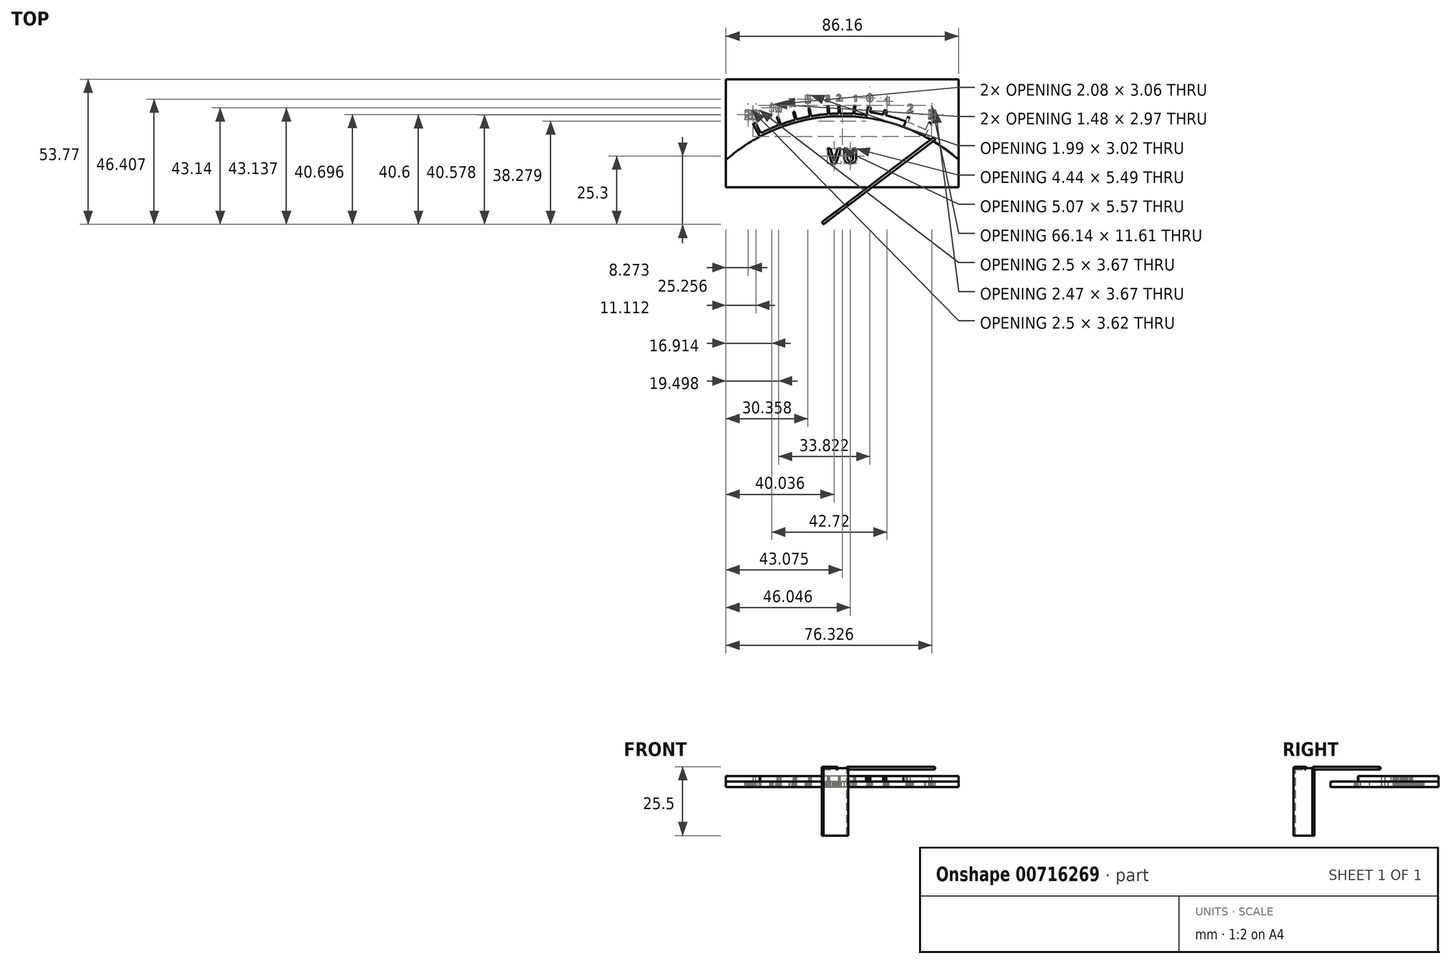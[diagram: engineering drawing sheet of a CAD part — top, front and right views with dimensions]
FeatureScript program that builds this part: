
annotation { "Feature Type Name" : "Feature", "Feature Type Description" : "" }
export const myFeature = defineFeature(function(context is Context, id is Id, definition is map)
    precondition{}
    {
        {
            var Q0;
            Q0=qCreatedBy(makeId("Top.planeOp"),FACE);
            var sketch = newSketch(context, id + "F0", { "sketchPlane" : qUnion([Q0])});
            skLineSegment(sketch, "E0.bottom", {"start": v(-47.11, 47.11) * mm, "end": v(47.11, 47.11) * mm, "construction": true});
            skLineSegment(sketch, "E0.top", {"start": v(-47.11, -47.11) * mm, "end": v(47.11, -47.11) * mm, "construction": true});
            skLineSegment(sketch, "E0.left", {"start": v(-47.11, 47.11) * mm, "end": v(-47.11, -47.11) * mm, "construction": true});
            skLineSegment(sketch, "E0.right", {"start": v(51.21, 42.43) * mm, "end": v(51.21, -51.8) * mm, "construction": true});
            skLineSegment(sketch, "E1", {"start": v(0, 0) * mm, "end": v(0, 47.11) * mm, "construction": true});
            skLineSegment(sketch, "E2.bottom", {"start": v(-43.08, 19.18) * mm, "end": v(43.08, 19.18) * mm});
            skLineSegment(sketch, "E2.top", {"start": v(-43.08, -20.84) * mm, "end": v(43.08, -20.84) * mm});
            skLineSegment(sketch, "E2.left", {"start": v(-43.08, 19.18) * mm, "end": v(-43.08, -20.84) * mm});
            skLineSegment(sketch, "E2.right", {"start": v(43.08, 19.18) * mm, "end": v(43.08, -20.84) * mm});
            skLineSegment(sketch, "E3", {"start": v(0, 0) * mm, "end": v(0, 19.18) * mm});
            skLineSegment(sketch, "E4", {"start": v(-43.08, -6.5) * mm, "end": v(-5.58, -6.5) * mm, "construction": true});
            skLineSegment(sketch, "E5", {"start": v(-31.08, 0) * mm, "end": v(-43.08, 0) * mm});
            skText(sketch, "E6", { "text": "V", "fontName": "OpenSans-Bold.ttf"});
            skText(sketch, "E7", { "text": "U", "fontName": "OpenSans-Bold.ttf"});
            skLineSegment(sketch, "E8", {"start": v(0, -6.5) * mm, "end": v(0.1, -6.5) * mm});
            skLineSegment(sketch, "E9", {"start": v(42.92, 0) * mm, "end": v(30.92, 0) * mm});
            skLineSegment(sketch, "E10", {"start": v(-33.08, 19.18) * mm, "end": v(-33.08, -21) * mm, "construction": true});
            skLineSegment(sketch, "E11", {"start": v(-23.08, 19.18) * mm, "end": v(-23.08, -21) * mm, "construction": true});
            skLineSegment(sketch, "E12", {"start": v(-13.08, 19.18) * mm, "end": v(-13.08, -21) * mm, "construction": true});
            skLineSegment(sketch, "E13", {"start": v(-3.08, 19.18) * mm, "end": v(-3.08, -21) * mm, "construction": true});
            skLineSegment(sketch, "E14", {"start": v(6.92, 19.18) * mm, "end": v(6.92, -21) * mm, "construction": true});
            skLineSegment(sketch, "E15", {"start": v(16.92, 19.18) * mm, "end": v(16.92, -21) * mm, "construction": true});
            skLineSegment(sketch, "E16", {"start": v(26.92, 19.18) * mm, "end": v(26.92, -20.84) * mm, "construction": true});
            skLineSegment(sketch, "E17", {"start": v(36.92, 19.18) * mm, "end": v(36.92, -20.84) * mm, "construction": true});
            skLineSegment(sketch, "E18", {"start": v(-43.08, 9.18) * mm, "end": v(42.92, 9.18) * mm, "construction": true});
            skLineSegment(sketch, "E19", {"start": v(-43.08, -0.82) * mm, "end": v(42.92, -0.82) * mm, "construction": true});
            skLineSegment(sketch, "E20", {"start": v(-43.08, -10.82) * mm, "end": v(42.92, -10.82) * mm, "construction": true});
            skLineSegment(sketch, "E21", {"start": v(0, 0) * mm, "end": v(0.1, -60) * mm});
            skCircle(sketch, "E22", {"center": v(0.1, -60) * mm, "radius": 65.5 * mm});
            skCircle(sketch, "E23", {"center": v(0.1, -60) * mm, "radius": 66.5 * mm});
            skLineSegment(sketch, "E24", {"start": v(0.1, -60) * mm, "end": v(-33.08, 2.65) * mm});
            skLineSegment(sketch, "E25", {"start": v(0.1, -60) * mm, "end": v(-32.19, 3.1) * mm});
            skCircle(sketch, "E26", {"center": v(0.1, -60) * mm, "radius": 70.89 * mm});
            skLineSegment(sketch, "E27", {"start": v(0.1, -60) * mm, "end": v(33.07, 2.76) * mm});
            skLineSegment(sketch, "E28", {"start": v(0.1, -60) * mm, "end": v(32.18, 3.22) * mm});
            skCircle(sketch, "E29", {"center": v(0.1, -60) * mm, "radius": 67.75 * mm});
            skCircle(sketch, "E30", {"center": v(0.1, -60) * mm, "radius": 69.5 * mm});
            skLineSegment(sketch, "E31", {"start": v(0.1, -60) * mm, "end": v(9.42, 8.87) * mm});
            skLineSegment(sketch, "E32", {"start": v(0.1, -60) * mm, "end": v(10.62, 8.7) * mm});
            skLineSegment(sketch, "E33", {"start": v(0.1, -60) * mm, "end": v(-24.25, 5.1) * mm});
            skLineSegment(sketch, "E34", {"start": v(0.1, -60) * mm, "end": v(-23.78, 5.27) * mm});
            skLineSegment(sketch, "E35", {"start": v(0.1, -60) * mm, "end": v(-18.25, 7.03) * mm});
            skLineSegment(sketch, "E36", {"start": v(0.1, -60) * mm, "end": v(-17.77, 7.16) * mm});
            skLineSegment(sketch, "E37", {"start": v(0.1, -60) * mm, "end": v(-12.08, 8.42) * mm});
            skLineSegment(sketch, "E38", {"start": v(-12.57, 8.33) * mm, "end": v(0.1, -60) * mm});
            skLineSegment(sketch, "E39", {"start": v(0.1, -60) * mm, "end": v(-5.49, 9.27) * mm});
            skLineSegment(sketch, "E40", {"start": v(0.1, -60) * mm, "end": v(-5, 9.31) * mm});
            skLineSegment(sketch, "E41", {"start": v(0.1, -60) * mm, "end": v(-1.42, 9.48) * mm});
            skLineSegment(sketch, "E42", {"start": v(0.1, -60) * mm, "end": v(-0.92, 9.5) * mm});
            skLineSegment(sketch, "E43", {"start": v(0.1, -60) * mm, "end": v(4.35, 9.37) * mm});
            skLineSegment(sketch, "E44", {"start": v(0.1, -60) * mm, "end": v(4.85, 9.34) * mm});
            skLineSegment(sketch, "E45", {"start": v(0.1, -60) * mm, "end": v(15.62, 7.74) * mm});
            skLineSegment(sketch, "E46", {"start": v(0.1, -60) * mm, "end": v(16.6, 7.51) * mm});
            skLineSegment(sketch, "E47", {"start": v(0.1, -60) * mm, "end": v(24.1, 5.23) * mm});
            skLineSegment(sketch, "E48", {"start": v(0.1, -60) * mm, "end": v(25.03, 4.87) * mm});
            skCircle(sketch, "E49", {"center": v(0.1, -60) * mm, "radius": 71.64 * mm, "construction": true});
            const initialGuessF0  = {"E6": [-0.00558, -0.01212, 1, 0, 0.00562], "E7": [0.0001, -0.01196, 1, 0, 0.00546]};
            skSetInitialGuess(sketch, initialGuessF0);
            skSolve(sketch);
        }
        {
            var Q0;
            {var subQ0=sQuery(id+"F0.wireOp",EDGE,"E2.left");var subQ1=sQuery(id+"F0.wireOp",EDGE,"E2.top");var subQ2=makeQuery(id+"F0.imprint","INTERSECT",VERTEX,{"derivedFrom":[subQ1,subQ0]});Q0=makeQuery(id+"F0.imprint","IMPRINT",FACE,{"disambiguationData":[TD([[makeQuery(id+"F0.imprint","IMPRINT",EDGE,{"disambiguationData":[TD([[subQ2,-1.0]])],"derivedFrom":subQ1}),1.0]])]});}
            var Q1;
            Q1=makeQuery(id+"F0.imprint","IMPRINT",FACE,{"disambiguationData":[TD([[makeQuery(id+"F0.imprint","IMPRINT",EDGE,{"derivedFrom":sQuery(id+"F0.wireOp",EDGE,"E6.sketch_text.stroke-0")}),1.0]])]});
            var Q2;
            {var subQ0=sQuery(id+"F0.wireOp",EDGE,"E23");var subQ1=sQuery(id+"F0.wireOp",EDGE,"E2.left");var subQ2=makeQuery(id+"F0.imprint","INTERSECT",VERTEX,{"derivedFrom":[subQ1,subQ0]});Q2=makeQuery(id+"F0.imprint","IMPRINT",FACE,{"disambiguationData":[TD([[makeQuery(id+"F0.imprint","IMPRINT",EDGE,{"disambiguationData":[TD([[subQ2,-1.0]])],"derivedFrom":subQ1}),1.0]])]});}
            var Q3;
            {var subQ5=sQuery(id+"F0.wireOp",EDGE,"E26");var subQ6=sQuery(id+"F0.wireOp",EDGE,"E2.left");var subQ7=makeQuery(id+"F0.imprint","INTERSECT",VERTEX,{"derivedFrom":[subQ6,subQ5]});Q3=makeQuery(id+"F0.imprint","IMPRINT",FACE,{"disambiguationData":[TD([[makeQuery(id+"F0.imprint","IMPRINT",EDGE,{"disambiguationData":[TD([[subQ7,-1.0]])],"derivedFrom":subQ6}),1.0]])]});}
            var Q4;
            {var subQ1=sQuery(id+"F0.wireOp",EDGE,"E2.left");var subQ5=sQuery(id+"F0.wireOp",EDGE,"E2.bottom");var subQ6=makeQuery(id+"F0.imprint","INTERSECT",VERTEX,{"derivedFrom":[subQ5,subQ1]});Q4=makeQuery(id+"F0.imprint","IMPRINT",FACE,{"disambiguationData":[TD([[makeQuery(id+"F0.imprint","IMPRINT",EDGE,{"disambiguationData":[TD([[subQ6,-1.0]])],"derivedFrom":subQ5}),-1.0]])]});}
            var Q5;
            {var subQ0=sQuery(id+"F0.wireOp",EDGE,"E23");var subQ1=sQuery(id+"F0.wireOp",EDGE,"E3");var subQ2=makeQuery(id+"F0.imprint","INTERSECT",VERTEX,{"derivedFrom":[subQ1,subQ0]});Q5=makeQuery(id+"F0.imprint","IMPRINT",FACE,{"disambiguationData":[TD([[makeQuery(id+"F0.imprint","IMPRINT",EDGE,{"disambiguationData":[TD([[subQ2,-1.0]])],"derivedFrom":subQ1}),1.0]])]});}
            var Q6;
            {var subQ0=sQuery(id+"F0.wireOp",EDGE,"E23");var subQ1=sQuery(id+"F0.wireOp",EDGE,"E3");var subQ2=makeQuery(id+"F0.imprint","INTERSECT",VERTEX,{"derivedFrom":[subQ1,subQ0]});Q6=makeQuery(id+"F0.imprint","IMPRINT",FACE,{"disambiguationData":[TD([[makeQuery(id+"F0.imprint","IMPRINT",EDGE,{"disambiguationData":[TD([[subQ2,-1.0]])],"derivedFrom":subQ1}),-1.0]])]});}
            var Q7;
            Q7=makeQuery(id+"F0.imprint","IMPRINT",FACE,{"disambiguationData":[TD([[makeQuery(id+"F0.imprint","IMPRINT",EDGE,{"derivedFrom":sQuery(id+"F0.wireOp",EDGE,"E7.sketch_text.stroke-0")}),1.0]])]});
            var Q8;
            {var subQ0=sQuery(id+"F0.wireOp",EDGE,"E2.right");var subQ1=sQuery(id+"F0.wireOp",EDGE,"E2.top");var subQ2=makeQuery(id+"F0.imprint","INTERSECT",VERTEX,{"derivedFrom":[subQ1,subQ0]});Q8=makeQuery(id+"F0.imprint","IMPRINT",FACE,{"disambiguationData":[TD([[makeQuery(id+"F0.imprint","IMPRINT",EDGE,{"disambiguationData":[TD([[subQ2,1.0]])],"derivedFrom":subQ1}),1.0]])]});}
            var Q9;
            {var subQ0=sQuery(id+"F0.wireOp",EDGE,"E26");var subQ6=sQuery(id+"F0.wireOp",EDGE,"E2.right");var subQ9=makeQuery(id+"F0.imprint","INTERSECT",VERTEX,{"derivedFrom":[subQ6,subQ0]});Q9=makeQuery(id+"F0.imprint","IMPRINT",FACE,{"disambiguationData":[TD([[makeQuery(id+"F0.imprint","IMPRINT",EDGE,{"disambiguationData":[TD([[subQ9,-1.0]])],"derivedFrom":subQ6}),-1.0]])]});}
            var Q10;
            {var subQ0=sQuery(id+"F0.wireOp",EDGE,"E23");var subQ1=sQuery(id+"F0.wireOp",EDGE,"E2.right");var subQ2=makeQuery(id+"F0.imprint","INTERSECT",VERTEX,{"derivedFrom":[subQ1,subQ0]});Q10=makeQuery(id+"F0.imprint","IMPRINT",FACE,{"disambiguationData":[TD([[makeQuery(id+"F0.imprint","IMPRINT",EDGE,{"disambiguationData":[TD([[subQ2,-1.0]])],"derivedFrom":subQ1}),-1.0]])]});}
            var Q11;
            {var subQ0=sQuery(id+"F0.wireOp",EDGE,"E26");var subQ1=sQuery(id+"F0.wireOp",EDGE,"E9");var subQ2=makeQuery(id+"F0.imprint","INTERSECT",VERTEX,{"derivedFrom":[subQ1,subQ0]});Q11=makeQuery(id+"F0.imprint","IMPRINT",FACE,{"disambiguationData":[TD([[makeQuery(id+"F0.imprint","IMPRINT",EDGE,{"disambiguationData":[TD([[subQ2,-1.0]])],"derivedFrom":subQ1}),-1.0]])]});}
            var Q12;
            {var subQ1=sQuery(id+"F0.wireOp",EDGE,"E2.right");var subQ5=sQuery(id+"F0.wireOp",EDGE,"E2.bottom");var subQ9=makeQuery(id+"F0.imprint","INTERSECT",VERTEX,{"derivedFrom":[subQ5,subQ1]});Q12=makeQuery(id+"F0.imprint","IMPRINT",FACE,{"disambiguationData":[TD([[makeQuery(id+"F0.imprint","IMPRINT",EDGE,{"disambiguationData":[TD([[subQ9,1.0]])],"derivedFrom":subQ5}),-1.0]])]});}
            var Q13;
            {var subQ0=sQuery(id+"F0.wireOp",EDGE,"E5");var subQ1=sQuery(id+"F0.wireOp",EDGE,"E2.left");var subQ2=makeQuery(id+"F0.imprint","INTERSECT",VERTEX,{"derivedFrom":[subQ1,subQ0]});Q13=makeQuery(id+"F0.imprint","IMPRINT",FACE,{"disambiguationData":[TD([[makeQuery(id+"F0.imprint","IMPRINT",EDGE,{"disambiguationData":[TD([[subQ2,-1.0]])],"derivedFrom":subQ1}),1.0]])]});}
            var Q14;
            {var subQ0=sQuery(id+"F0.wireOp",EDGE,"E24");var subQ1=sQuery(id+"F0.wireOp",EDGE,"E5");var subQ2=makeQuery(id+"F0.imprint","INTERSECT",VERTEX,{"derivedFrom":[subQ1,subQ0]});Q14=makeQuery(id+"F0.imprint","IMPRINT",FACE,{"disambiguationData":[TD([[makeQuery(id+"F0.imprint","IMPRINT",EDGE,{"disambiguationData":[TD([[subQ2,-1.0]])],"derivedFrom":subQ1}),-1.0]])]});}
            var Q15;
            {var subQ0=sQuery(id+"F0.wireOp",EDGE,"E28");var subQ1=sQuery(id+"F0.wireOp",EDGE,"E2.top");var subQ2=makeQuery(id+"F0.imprint","INTERSECT",VERTEX,{"derivedFrom":[subQ1,subQ0]});Q15=makeQuery(id+"F0.imprint","IMPRINT",FACE,{"disambiguationData":[TD([[makeQuery(id+"F0.imprint","IMPRINT",EDGE,{"disambiguationData":[TD([[subQ2,-1.0]])],"derivedFrom":subQ1}),1.0]])]});}
            var Q16;
            {var subQ0=sQuery(id+"F0.wireOp",EDGE,"E24");var subQ1=sQuery(id+"F0.wireOp",EDGE,"E2.top");var subQ2=makeQuery(id+"F0.imprint","INTERSECT",VERTEX,{"derivedFrom":[subQ1,subQ0]});Q16=makeQuery(id+"F0.imprint","IMPRINT",FACE,{"disambiguationData":[TD([[makeQuery(id+"F0.imprint","IMPRINT",EDGE,{"disambiguationData":[TD([[subQ2,-1.0]])],"derivedFrom":subQ1}),1.0]])]});}
            var Q17;
            {var subQ0=sQuery(id+"F0.wireOp",EDGE,"E29");var subQ1=sQuery(id+"F0.wireOp",EDGE,"E2.right");var subQ2=makeQuery(id+"F0.imprint","INTERSECT",VERTEX,{"derivedFrom":[subQ1,subQ0]});Q17=makeQuery(id+"F0.imprint","IMPRINT",FACE,{"disambiguationData":[TD([[makeQuery(id+"F0.imprint","IMPRINT",EDGE,{"disambiguationData":[TD([[subQ2,-1.0]])],"derivedFrom":subQ1}),-1.0]])]});}
            var Q18;
            {var subQ1=sQuery(id+"F0.wireOp",EDGE,"E2.right");var subQ7=sQuery(id+"F0.wireOp",EDGE,"E30");var subQ9=makeQuery(id+"F0.imprint","INTERSECT",VERTEX,{"derivedFrom":[subQ1,subQ7]});Q18=makeQuery(id+"F0.imprint","IMPRINT",FACE,{"disambiguationData":[TD([[makeQuery(id+"F0.imprint","IMPRINT",EDGE,{"disambiguationData":[TD([[subQ9,-1.0]])],"derivedFrom":subQ1}),-1.0]])]});}
            var Q19;
            {var subQ0=sQuery(id+"F0.wireOp",EDGE,"E30");var subQ1=sQuery(id+"F0.wireOp",EDGE,"E9");var subQ2=makeQuery(id+"F0.imprint","INTERSECT",VERTEX,{"derivedFrom":[subQ1,subQ0]});Q19=makeQuery(id+"F0.imprint","IMPRINT",FACE,{"disambiguationData":[TD([[makeQuery(id+"F0.imprint","IMPRINT",EDGE,{"disambiguationData":[TD([[subQ2,-1.0]])],"derivedFrom":subQ1}),-1.0]])]});}
            var Q20;
            {var subQ0=sQuery(id+"F0.wireOp",EDGE,"E30");var subQ1=sQuery(id+"F0.wireOp",EDGE,"E3");var subQ2=makeQuery(id+"F0.imprint","INTERSECT",VERTEX,{"derivedFrom":[subQ1,subQ0]});Q20=makeQuery(id+"F0.imprint","IMPRINT",FACE,{"disambiguationData":[TD([[makeQuery(id+"F0.imprint","IMPRINT",EDGE,{"disambiguationData":[TD([[subQ2,-1.0]])],"derivedFrom":subQ1}),-1.0]])]});}
            var Q21;
            {var subQ0=sQuery(id+"F0.wireOp",EDGE,"E29");var subQ1=sQuery(id+"F0.wireOp",EDGE,"E3");var subQ2=makeQuery(id+"F0.imprint","INTERSECT",VERTEX,{"derivedFrom":[subQ1,subQ0]});Q21=makeQuery(id+"F0.imprint","IMPRINT",FACE,{"disambiguationData":[TD([[makeQuery(id+"F0.imprint","IMPRINT",EDGE,{"disambiguationData":[TD([[subQ2,-1.0]])],"derivedFrom":subQ1}),-1.0]])]});}
            var Q22;
            {var subQ5=sQuery(id+"F0.wireOp",EDGE,"E2.left");var subQ7=sQuery(id+"F0.wireOp",EDGE,"E30");var subQ9=makeQuery(id+"F0.imprint","INTERSECT",VERTEX,{"derivedFrom":[subQ5,subQ7]});Q22=makeQuery(id+"F0.imprint","IMPRINT",FACE,{"disambiguationData":[TD([[makeQuery(id+"F0.imprint","IMPRINT",EDGE,{"disambiguationData":[TD([[subQ9,-1.0]])],"derivedFrom":subQ5}),1.0]])]});}
            var Q23;
            {var subQ0=sQuery(id+"F0.wireOp",EDGE,"E29");var subQ1=sQuery(id+"F0.wireOp",EDGE,"E2.left");var subQ2=makeQuery(id+"F0.imprint","INTERSECT",VERTEX,{"derivedFrom":[subQ1,subQ0]});Q23=makeQuery(id+"F0.imprint","IMPRINT",FACE,{"disambiguationData":[TD([[makeQuery(id+"F0.imprint","IMPRINT",EDGE,{"disambiguationData":[TD([[subQ2,-1.0]])],"derivedFrom":subQ1}),1.0]])]});}
            var Q24;
            {var subQ0=sQuery(id+"F0.wireOp",EDGE,"E30");var subQ1=sQuery(id+"F0.wireOp",EDGE,"E5");var subQ2=makeQuery(id+"F0.imprint","INTERSECT",VERTEX,{"derivedFrom":[subQ1,subQ0]});Q24=makeQuery(id+"F0.imprint","IMPRINT",FACE,{"disambiguationData":[TD([[makeQuery(id+"F0.imprint","IMPRINT",EDGE,{"disambiguationData":[TD([[subQ2,-1.0]])],"derivedFrom":subQ1}),-1.0]])]});}
            var Q25;
            {var subQ0=sQuery(id+"F0.wireOp",EDGE,"E29");var subQ1=sQuery(id+"F0.wireOp",EDGE,"E3");var subQ2=makeQuery(id+"F0.imprint","INTERSECT",VERTEX,{"derivedFrom":[subQ1,subQ0]});Q25=makeQuery(id+"F0.imprint","IMPRINT",FACE,{"disambiguationData":[TD([[makeQuery(id+"F0.imprint","IMPRINT",EDGE,{"disambiguationData":[TD([[subQ2,-1.0]])],"derivedFrom":subQ1}),1.0]])]});}
            var Q26;
            {var subQ0=sQuery(id+"F0.wireOp",EDGE,"E30");var subQ1=sQuery(id+"F0.wireOp",EDGE,"E3");var subQ2=makeQuery(id+"F0.imprint","INTERSECT",VERTEX,{"derivedFrom":[subQ1,subQ0]});Q26=makeQuery(id+"F0.imprint","IMPRINT",FACE,{"disambiguationData":[TD([[makeQuery(id+"F0.imprint","IMPRINT",EDGE,{"disambiguationData":[TD([[subQ2,-1.0]])],"derivedFrom":subQ1}),1.0]])]});}
            var Q27;
            {var subQ0=sQuery(id+"F0.wireOp",EDGE,"E32");var subQ1=sQuery(id+"F0.wireOp",EDGE,"E2.top");var subQ2=makeQuery(id+"F0.imprint","INTERSECT",VERTEX,{"derivedFrom":[subQ1,subQ0]});Q27=makeQuery(id+"F0.imprint","IMPRINT",FACE,{"disambiguationData":[TD([[makeQuery(id+"F0.imprint","IMPRINT",EDGE,{"disambiguationData":[TD([[subQ2,-1.0]])],"derivedFrom":subQ1}),1.0]])]});}
            var Q28;
            {var subQ0=sQuery(id+"F0.wireOp",EDGE,"E29");var subQ1=sQuery(id+"F0.wireOp",EDGE,"E28");var subQ2=makeQuery(id+"F0.imprint","INTERSECT",VERTEX,{"derivedFrom":[subQ1,subQ0]});Q28=makeQuery(id+"F0.imprint","IMPRINT",FACE,{"disambiguationData":[TD([[makeQuery(id+"F0.imprint","IMPRINT",EDGE,{"disambiguationData":[TD([[subQ2,-1.0]])],"derivedFrom":subQ1}),1.0]])]});}
            var Q29;
            {var subQ0=sQuery(id+"F0.wireOp",EDGE,"E31");var subQ1=sQuery(id+"F0.wireOp",EDGE,"E2.top");var subQ2=makeQuery(id+"F0.imprint","INTERSECT",VERTEX,{"derivedFrom":[subQ1,subQ0]});Q29=makeQuery(id+"F0.imprint","IMPRINT",FACE,{"disambiguationData":[TD([[makeQuery(id+"F0.imprint","IMPRINT",EDGE,{"disambiguationData":[TD([[subQ2,-1.0]])],"derivedFrom":subQ1}),1.0]])]});}
            var Q30;
            {var subQ0=sQuery(id+"F0.wireOp",EDGE,"E25");var subQ1=sQuery(id+"F0.wireOp",EDGE,"E2.top");var subQ2=makeQuery(id+"F0.imprint","INTERSECT",VERTEX,{"derivedFrom":[subQ1,subQ0]});Q30=makeQuery(id+"F0.imprint","IMPRINT",FACE,{"disambiguationData":[TD([[makeQuery(id+"F0.imprint","IMPRINT",EDGE,{"disambiguationData":[TD([[subQ2,-1.0]])],"derivedFrom":subQ1}),1.0]])]});}
            var Q31;
            {var subQ0=sQuery(id+"F0.wireOp",EDGE,"E33");var subQ1=sQuery(id+"F0.wireOp",EDGE,"E2.top");var subQ2=makeQuery(id+"F0.imprint","INTERSECT",VERTEX,{"derivedFrom":[subQ1,subQ0]});Q31=makeQuery(id+"F0.imprint","IMPRINT",FACE,{"disambiguationData":[TD([[makeQuery(id+"F0.imprint","IMPRINT",EDGE,{"disambiguationData":[TD([[subQ2,-1.0]])],"derivedFrom":subQ1}),1.0]])]});}
            var Q32;
            {var subQ0=sQuery(id+"F0.wireOp",EDGE,"E33");var subQ1=sQuery(id+"F0.wireOp",EDGE,"E23");var subQ2=makeQuery(id+"F0.imprint","INTERSECT",VERTEX,{"derivedFrom":[subQ1,subQ0]});Q32=makeQuery(id+"F0.imprint","IMPRINT",FACE,{"disambiguationData":[TD([[makeQuery(id+"F0.imprint","IMPRINT",EDGE,{"disambiguationData":[TD([[subQ2,-1.0]])],"derivedFrom":subQ1}),-1.0]])]});}
            var Q33;
            {var subQ0=sQuery(id+"F0.wireOp",EDGE,"E29");var subQ1=sQuery(id+"F0.wireOp",EDGE,"E25");var subQ2=makeQuery(id+"F0.imprint","INTERSECT",VERTEX,{"derivedFrom":[subQ1,subQ0]});Q33=makeQuery(id+"F0.imprint","IMPRINT",FACE,{"disambiguationData":[TD([[makeQuery(id+"F0.imprint","IMPRINT",EDGE,{"disambiguationData":[TD([[subQ2,-1.0]])],"derivedFrom":subQ1}),-1.0]])]});}
            var Q34;
            {var subQ0=sQuery(id+"F0.wireOp",EDGE,"E34");var subQ1=sQuery(id+"F0.wireOp",EDGE,"E2.top");var subQ2=makeQuery(id+"F0.imprint","INTERSECT",VERTEX,{"derivedFrom":[subQ1,subQ0]});Q34=makeQuery(id+"F0.imprint","IMPRINT",FACE,{"disambiguationData":[TD([[makeQuery(id+"F0.imprint","IMPRINT",EDGE,{"disambiguationData":[TD([[subQ2,-1.0]])],"derivedFrom":subQ1}),1.0]])]});}
            var Q35;
            {var subQ0=sQuery(id+"F0.wireOp",EDGE,"E35");var subQ1=sQuery(id+"F0.wireOp",EDGE,"E2.top");var subQ2=makeQuery(id+"F0.imprint","INTERSECT",VERTEX,{"derivedFrom":[subQ1,subQ0]});Q35=makeQuery(id+"F0.imprint","IMPRINT",FACE,{"disambiguationData":[TD([[makeQuery(id+"F0.imprint","IMPRINT",EDGE,{"disambiguationData":[TD([[subQ2,-1.0]])],"derivedFrom":subQ1}),1.0]])]});}
            var Q36;
            {var subQ0=sQuery(id+"F0.wireOp",EDGE,"E35");var subQ1=sQuery(id+"F0.wireOp",EDGE,"E29");var subQ2=makeQuery(id+"F0.imprint","INTERSECT",VERTEX,{"derivedFrom":[subQ1,subQ0]});Q36=makeQuery(id+"F0.imprint","IMPRINT",FACE,{"disambiguationData":[TD([[makeQuery(id+"F0.imprint","IMPRINT",EDGE,{"disambiguationData":[TD([[subQ2,-1.0]])],"derivedFrom":subQ1}),-1.0]])]});}
            var Q37;
            {var subQ0=sQuery(id+"F0.wireOp",EDGE,"E35");var subQ1=sQuery(id+"F0.wireOp",EDGE,"E23");var subQ2=makeQuery(id+"F0.imprint","INTERSECT",VERTEX,{"derivedFrom":[subQ1,subQ0]});Q37=makeQuery(id+"F0.imprint","IMPRINT",FACE,{"disambiguationData":[TD([[makeQuery(id+"F0.imprint","IMPRINT",EDGE,{"disambiguationData":[TD([[subQ2,-1.0]])],"derivedFrom":subQ1}),-1.0]])]});}
            var Q38;
            {var subQ0=sQuery(id+"F0.wireOp",EDGE,"E36");var subQ1=sQuery(id+"F0.wireOp",EDGE,"E2.top");var subQ2=makeQuery(id+"F0.imprint","INTERSECT",VERTEX,{"derivedFrom":[subQ1,subQ0]});Q38=makeQuery(id+"F0.imprint","IMPRINT",FACE,{"disambiguationData":[TD([[makeQuery(id+"F0.imprint","IMPRINT",EDGE,{"disambiguationData":[TD([[subQ2,-1.0]])],"derivedFrom":subQ1}),1.0]])]});}
            var Q39;
            {var subQ0=sQuery(id+"F0.wireOp",EDGE,"E38");var subQ1=sQuery(id+"F0.wireOp",EDGE,"E29");var subQ2=makeQuery(id+"F0.imprint","INTERSECT",VERTEX,{"derivedFrom":[subQ1,subQ0]});Q39=makeQuery(id+"F0.imprint","IMPRINT",FACE,{"disambiguationData":[TD([[makeQuery(id+"F0.imprint","IMPRINT",EDGE,{"disambiguationData":[TD([[subQ2,-1.0]])],"derivedFrom":subQ1}),-1.0]])]});}
            var Q40;
            {var subQ0=sQuery(id+"F0.wireOp",EDGE,"E38");var subQ1=sQuery(id+"F0.wireOp",EDGE,"E23");var subQ2=makeQuery(id+"F0.imprint","INTERSECT",VERTEX,{"derivedFrom":[subQ1,subQ0]});Q40=makeQuery(id+"F0.imprint","IMPRINT",FACE,{"disambiguationData":[TD([[makeQuery(id+"F0.imprint","IMPRINT",EDGE,{"disambiguationData":[TD([[subQ2,-1.0]])],"derivedFrom":subQ1}),-1.0]])]});}
            var Q41;
            {var subQ0=sQuery(id+"F0.wireOp",EDGE,"E38");var subQ1=sQuery(id+"F0.wireOp",EDGE,"E2.top");var subQ2=makeQuery(id+"F0.imprint","INTERSECT",VERTEX,{"derivedFrom":[subQ1,subQ0]});Q41=makeQuery(id+"F0.imprint","IMPRINT",FACE,{"disambiguationData":[TD([[makeQuery(id+"F0.imprint","IMPRINT",EDGE,{"disambiguationData":[TD([[subQ2,-1.0]])],"derivedFrom":subQ1}),1.0]])]});}
            var Q42;
            {var subQ1=sQuery(id+"F0.wireOp",EDGE,"E6.sketch_text.stroke-4");Q42=makeQuery(id+"F0.imprint","IMPRINT",FACE,{"disambiguationData":[TD([[makeQuery(id+"F0.imprint","IMPRINT",EDGE,{"derivedFrom":subQ1}),1.0]])]});}
            var Q43;
            {var subQ0=sQuery(id+"F0.wireOp",EDGE,"E39");var subQ1=sQuery(id+"F0.wireOp",EDGE,"E6.sketch_text.stroke-5");var subQ2=makeQuery(id+"F0.imprint","INTERSECT",VERTEX,{"derivedFrom":[subQ1,subQ0]});Q43=makeQuery(id+"F0.imprint","IMPRINT",FACE,{"disambiguationData":[TD([[makeQuery(id+"F0.imprint","IMPRINT",EDGE,{"disambiguationData":[TD([[subQ2,-1.0]])],"derivedFrom":subQ1}),1.0]])]});}
            var Q44;
            {var subQ3=sQuery(id+"F0.wireOp",EDGE,"E39");var subQ5=sQuery(id+"F0.wireOp",EDGE,"E2.top");var subQ6=makeQuery(id+"F0.imprint","INTERSECT",VERTEX,{"derivedFrom":[subQ5,subQ3]});Q44=makeQuery(id+"F0.imprint","IMPRINT",FACE,{"disambiguationData":[TD([[makeQuery(id+"F0.imprint","IMPRINT",EDGE,{"disambiguationData":[TD([[subQ6,-1.0]])],"derivedFrom":subQ5}),1.0]])]});}
            var Q45;
            {var subQ0=sQuery(id+"F0.wireOp",EDGE,"E39");var subQ1=sQuery(id+"F0.wireOp",EDGE,"E29");var subQ2=makeQuery(id+"F0.imprint","INTERSECT",VERTEX,{"derivedFrom":[subQ1,subQ0]});Q45=makeQuery(id+"F0.imprint","IMPRINT",FACE,{"disambiguationData":[TD([[makeQuery(id+"F0.imprint","IMPRINT",EDGE,{"disambiguationData":[TD([[subQ2,-1.0]])],"derivedFrom":subQ1}),-1.0]])]});}
            var Q46;
            {var subQ0=sQuery(id+"F0.wireOp",EDGE,"E39");var subQ1=sQuery(id+"F0.wireOp",EDGE,"E23");var subQ2=makeQuery(id+"F0.imprint","INTERSECT",VERTEX,{"derivedFrom":[subQ1,subQ0]});Q46=makeQuery(id+"F0.imprint","IMPRINT",FACE,{"disambiguationData":[TD([[makeQuery(id+"F0.imprint","IMPRINT",EDGE,{"disambiguationData":[TD([[subQ2,-1.0]])],"derivedFrom":subQ1}),-1.0]])]});}
            var Q47;
            {var subQ0=sQuery(id+"F0.wireOp",EDGE,"E40");var subQ1=sQuery(id+"F0.wireOp",EDGE,"E2.top");var subQ2=makeQuery(id+"F0.imprint","INTERSECT",VERTEX,{"derivedFrom":[subQ1,subQ0]});Q47=makeQuery(id+"F0.imprint","IMPRINT",FACE,{"disambiguationData":[TD([[makeQuery(id+"F0.imprint","IMPRINT",EDGE,{"disambiguationData":[TD([[subQ2,-1.0]])],"derivedFrom":subQ1}),1.0]])]});}
            var Q48;
            {var subQ0=sQuery(id+"F0.wireOp",EDGE,"E6.sketch_text.stroke-6");Q48=makeQuery(id+"F0.imprint","IMPRINT",FACE,{"disambiguationData":[TD([[makeQuery(id+"F0.imprint","IMPRINT",EDGE,{"derivedFrom":subQ0}),1.0]])]});}
            var Q49;
            {var subQ0=sQuery(id+"F0.wireOp",EDGE,"E41");var subQ1=sQuery(id+"F0.wireOp",EDGE,"E29");var subQ2=makeQuery(id+"F0.imprint","INTERSECT",VERTEX,{"derivedFrom":[subQ1,subQ0]});Q49=makeQuery(id+"F0.imprint","IMPRINT",FACE,{"disambiguationData":[TD([[makeQuery(id+"F0.imprint","IMPRINT",EDGE,{"disambiguationData":[TD([[subQ2,-1.0]])],"derivedFrom":subQ1}),-1.0]])]});}
            var Q50;
            {var subQ0=sQuery(id+"F0.wireOp",EDGE,"E41");var subQ1=sQuery(id+"F0.wireOp",EDGE,"E23");var subQ2=makeQuery(id+"F0.imprint","INTERSECT",VERTEX,{"derivedFrom":[subQ1,subQ0]});Q50=makeQuery(id+"F0.imprint","IMPRINT",FACE,{"disambiguationData":[TD([[makeQuery(id+"F0.imprint","IMPRINT",EDGE,{"disambiguationData":[TD([[subQ2,-1.0]])],"derivedFrom":subQ1}),-1.0]])]});}
            var Q51;
            {var subQ5=sQuery(id+"F0.wireOp",EDGE,"E21");var subQ8=makeQuery(id+"F0.imprint","IMPRINT",VERTEX,{"derivedFrom":subQ5});Q51=makeQuery(id+"F0.imprint","IMPRINT",FACE,{"disambiguationData":[TD([[makeQuery(id+"F0.imprint","IMPRINT",EDGE,{"disambiguationData":[TD([[subQ8,1.0]])],"derivedFrom":subQ5}),-1.0]])]});}
            var Q52;
            {var subQ0=sQuery(id+"F0.wireOp",EDGE,"E41");var subQ1=sQuery(id+"F0.wireOp",EDGE,"E2.top");var subQ2=makeQuery(id+"F0.imprint","INTERSECT",VERTEX,{"derivedFrom":[subQ1,subQ0]});Q52=makeQuery(id+"F0.imprint","IMPRINT",FACE,{"disambiguationData":[TD([[makeQuery(id+"F0.imprint","IMPRINT",EDGE,{"disambiguationData":[TD([[subQ2,-1.0]])],"derivedFrom":subQ1}),1.0]])]});}
            var Q53;
            {var subQ15=sQuery(id+"F0.wireOp",EDGE,"E7.sketch_text.stroke-4");Q53=makeQuery(id+"F0.imprint","IMPRINT",FACE,{"disambiguationData":[TD([[makeQuery(id+"F0.imprint","IMPRINT",EDGE,{"derivedFrom":subQ15}),1.0]])]});}
            var Q54;
            {var subQ0=sQuery(id+"F0.wireOp",EDGE,"E43");var subQ1=sQuery(id+"F0.wireOp",EDGE,"E7.sketch_text.stroke-11");var subQ2=makeQuery(id+"F0.imprint","INTERSECT",VERTEX,{"derivedFrom":[subQ1,subQ0]});Q54=makeQuery(id+"F0.imprint","IMPRINT",FACE,{"disambiguationData":[TD([[makeQuery(id+"F0.imprint","IMPRINT",EDGE,{"disambiguationData":[TD([[subQ2,-1.0]])],"derivedFrom":subQ1}),1.0]])]});}
            var Q55;
            {var subQ0=sQuery(id+"F0.wireOp",EDGE,"E43");var subQ1=sQuery(id+"F0.wireOp",EDGE,"E2.top");var subQ2=makeQuery(id+"F0.imprint","INTERSECT",VERTEX,{"derivedFrom":[subQ1,subQ0]});Q55=makeQuery(id+"F0.imprint","IMPRINT",FACE,{"disambiguationData":[TD([[makeQuery(id+"F0.imprint","IMPRINT",EDGE,{"disambiguationData":[TD([[subQ2,-1.0]])],"derivedFrom":subQ1}),1.0]])]});}
            var Q56;
            {var subQ0=sQuery(id+"F0.wireOp",EDGE,"E31");var subQ1=sQuery(id+"F0.wireOp",EDGE,"E29");var subQ2=makeQuery(id+"F0.imprint","INTERSECT",VERTEX,{"derivedFrom":[subQ1,subQ0]});Q56=makeQuery(id+"F0.imprint","IMPRINT",FACE,{"disambiguationData":[TD([[makeQuery(id+"F0.imprint","IMPRINT",EDGE,{"disambiguationData":[TD([[subQ2,-1.0]])],"derivedFrom":subQ1}),-1.0]])]});}
            var Q57;
            {var subQ0=sQuery(id+"F0.wireOp",EDGE,"E31");var subQ1=sQuery(id+"F0.wireOp",EDGE,"E23");var subQ2=makeQuery(id+"F0.imprint","INTERSECT",VERTEX,{"derivedFrom":[subQ1,subQ0]});Q57=makeQuery(id+"F0.imprint","IMPRINT",FACE,{"disambiguationData":[TD([[makeQuery(id+"F0.imprint","IMPRINT",EDGE,{"disambiguationData":[TD([[subQ2,-1.0]])],"derivedFrom":subQ1}),-1.0]])]});}
            var Q58;
            {var subQ0=sQuery(id+"F0.wireOp",EDGE,"E45");var subQ1=sQuery(id+"F0.wireOp",EDGE,"E29");var subQ2=makeQuery(id+"F0.imprint","INTERSECT",VERTEX,{"derivedFrom":[subQ1,subQ0]});Q58=makeQuery(id+"F0.imprint","IMPRINT",FACE,{"disambiguationData":[TD([[makeQuery(id+"F0.imprint","IMPRINT",EDGE,{"disambiguationData":[TD([[subQ2,-1.0]])],"derivedFrom":subQ1}),-1.0]])]});}
            var Q59;
            {var subQ0=sQuery(id+"F0.wireOp",EDGE,"E47");var subQ1=sQuery(id+"F0.wireOp",EDGE,"E29");var subQ2=makeQuery(id+"F0.imprint","INTERSECT",VERTEX,{"derivedFrom":[subQ1,subQ0]});Q59=makeQuery(id+"F0.imprint","IMPRINT",FACE,{"disambiguationData":[TD([[makeQuery(id+"F0.imprint","IMPRINT",EDGE,{"disambiguationData":[TD([[subQ2,-1.0]])],"derivedFrom":subQ1}),-1.0]])]});}
            var Q60;
            {var subQ0=sQuery(id+"F0.wireOp",EDGE,"E46");var subQ1=sQuery(id+"F0.wireOp",EDGE,"E2.top");var subQ2=makeQuery(id+"F0.imprint","INTERSECT",VERTEX,{"derivedFrom":[subQ1,subQ0]});Q60=makeQuery(id+"F0.imprint","IMPRINT",FACE,{"disambiguationData":[TD([[makeQuery(id+"F0.imprint","IMPRINT",EDGE,{"disambiguationData":[TD([[subQ2,-1.0]])],"derivedFrom":subQ1}),1.0]])]});}
            var Q61;
            {var subQ0=sQuery(id+"F0.wireOp",EDGE,"E48");var subQ1=sQuery(id+"F0.wireOp",EDGE,"E2.top");var subQ2=makeQuery(id+"F0.imprint","INTERSECT",VERTEX,{"derivedFrom":[subQ1,subQ0]});Q61=makeQuery(id+"F0.imprint","IMPRINT",FACE,{"disambiguationData":[TD([[makeQuery(id+"F0.imprint","IMPRINT",EDGE,{"disambiguationData":[TD([[subQ2,-1.0]])],"derivedFrom":subQ1}),1.0]])]});}
            var Q62;
            {var subQ0=sQuery(id+"F0.wireOp",EDGE,"E47");var subQ1=sQuery(id+"F0.wireOp",EDGE,"E2.top");var subQ2=makeQuery(id+"F0.imprint","INTERSECT",VERTEX,{"derivedFrom":[subQ1,subQ0]});Q62=makeQuery(id+"F0.imprint","IMPRINT",FACE,{"disambiguationData":[TD([[makeQuery(id+"F0.imprint","IMPRINT",EDGE,{"disambiguationData":[TD([[subQ2,-1.0]])],"derivedFrom":subQ1}),1.0]])]});}
            var Q63;
            {var subQ0=sQuery(id+"F0.wireOp",EDGE,"E45");var subQ1=sQuery(id+"F0.wireOp",EDGE,"E2.top");var subQ2=makeQuery(id+"F0.imprint","INTERSECT",VERTEX,{"derivedFrom":[subQ1,subQ0]});Q63=makeQuery(id+"F0.imprint","IMPRINT",FACE,{"disambiguationData":[TD([[makeQuery(id+"F0.imprint","IMPRINT",EDGE,{"disambiguationData":[TD([[subQ2,-1.0]])],"derivedFrom":subQ1}),1.0]])]});}
            var Q64;
            Q64=makeQuery(id+"F0.imprint","IMPRINT",FACE,{"disambiguationData":[TD([[makeQuery(id+"F0.imprint","IMPRINT",EDGE,{"derivedFrom":sQuery(id+"F0.wireOp",EDGE,"f8671e31-952e-4ee1-884e-408a6dc6b041.sketch_text.stroke-32")}),1.0]])]});
            extrude(context, id + "F1", {"entities" : qUnion([Q0, Q1, Q2, Q3, Q4, Q5, Q6, Q7, Q8, Q9, Q10, Q11, Q12, Q13, Q14, Q15, Q16, Q17, Q18, Q19, Q20, Q21, Q22, Q23, Q24, Q25, Q26, Q27, Q28, Q29, Q30, Q31, Q32, Q33, Q34, Q35, Q36, Q37, Q38, Q39, Q40, Q41, Q42, Q43, Q44, Q45, Q46, Q47, Q48, Q49, Q50, Q51, Q52, Q53, Q54, Q55, Q56, Q57, Q58, Q59, Q60, Q61, Q62, Q63, Q64]), "depth" : 2 * mm, "offsetDistance" : 25 * mm});
        }
        {
            var Q0;
            Q0=makeQuery(id+"F1.opExtrude","CAP_FACE",FACE,{"disambiguationData":[OSD([sQuery(id+"F0.wireOp",EDGE,"E2.bottom"),sQuery(id+"F0.wireOp",EDGE,"E2.top"),sQuery(id+"F0.wireOp",EDGE,"E2.left"),sQuery(id+"F0.wireOp",EDGE,"E2.right"),sQuery(id+"F0.wireOp",EDGE,"E6.sketch_text.stroke-0"),sQuery(id+"F0.wireOp",EDGE,"E6.sketch_text.stroke-1"),sQuery(id+"F0.wireOp",EDGE,"E6.sketch_text.stroke-2"),sQuery(id+"F0.wireOp",EDGE,"E6.sketch_text.stroke-3"),sQuery(id+"F0.wireOp",EDGE,"E6.sketch_text.stroke-4"),sQuery(id+"F0.wireOp",EDGE,"E6.sketch_text.stroke-5"),sQuery(id+"F0.wireOp",EDGE,"E6.sketch_text.stroke-6"),sQuery(id+"F0.wireOp",EDGE,"E6.sketch_text.stroke-7"),sQuery(id+"F0.wireOp",EDGE,"E6.sketch_text.stroke-8"),sQuery(id+"F0.wireOp",EDGE,"E6.sketch_text.stroke-9"),sQuery(id+"F0.wireOp",EDGE,"E7.sketch_text.stroke-0"),sQuery(id+"F0.wireOp",EDGE,"E7.sketch_text.stroke-1"),sQuery(id+"F0.wireOp",EDGE,"E7.sketch_text.stroke-2"),sQuery(id+"F0.wireOp",EDGE,"E7.sketch_text.stroke-3"),sQuery(id+"F0.wireOp",EDGE,"E7.sketch_text.stroke-4"),sQuery(id+"F0.wireOp",EDGE,"E7.sketch_text.stroke-5"),sQuery(id+"F0.wireOp",EDGE,"E7.sketch_text.stroke-6"),sQuery(id+"F0.wireOp",EDGE,"E7.sketch_text.stroke-7"),sQuery(id+"F0.wireOp",EDGE,"E7.sketch_text.stroke-8"),sQuery(id+"F0.wireOp",EDGE,"E7.sketch_text.stroke-9"),sQuery(id+"F0.wireOp",EDGE,"E7.sketch_text.stroke-10"),sQuery(id+"F0.wireOp",EDGE,"E7.sketch_text.stroke-11"),sQuery(id+"F0.wireOp",EDGE,"E7.sketch_text.stroke-12"),sQuery(id+"F0.wireOp",EDGE,"E7.sketch_text.stroke-13"),sQuery(id+"F0.wireOp",EDGE,"E7.sketch_text.stroke-14"),sQuery(id+"F0.wireOp",EDGE,"E22"),sQuery(id+"F0.wireOp",EDGE,"E23"),sQuery(id+"F0.wireOp",EDGE,"E24"),sQuery(id+"F0.wireOp",EDGE,"E25"),sQuery(id+"F0.wireOp",EDGE,"E26"),sQuery(id+"F0.wireOp",EDGE,"E27"),sQuery(id+"F0.wireOp",EDGE,"E28"),sQuery(id+"F0.wireOp",EDGE,"E29"),sQuery(id+"F0.wireOp",EDGE,"E30"),sQuery(id+"F0.wireOp",EDGE,"E31"),sQuery(id+"F0.wireOp",EDGE,"E32"),sQuery(id+"F0.wireOp",EDGE,"E33"),sQuery(id+"F0.wireOp",EDGE,"E34"),sQuery(id+"F0.wireOp",EDGE,"E35"),sQuery(id+"F0.wireOp",EDGE,"E36"),sQuery(id+"F0.wireOp",EDGE,"E37"),sQuery(id+"F0.wireOp",EDGE,"E38"),sQuery(id+"F0.wireOp",EDGE,"E39"),sQuery(id+"F0.wireOp",EDGE,"E40"),sQuery(id+"F0.wireOp",EDGE,"E41"),sQuery(id+"F0.wireOp",EDGE,"E42"),sQuery(id+"F0.wireOp",EDGE,"E43"),sQuery(id+"F0.wireOp",EDGE,"E44"),sQuery(id+"F0.wireOp",EDGE,"E45"),sQuery(id+"F0.wireOp",EDGE,"E46"),sQuery(id+"F0.wireOp",EDGE,"E47"),sQuery(id+"F0.wireOp",EDGE,"E48")])],"isStart":false});
            var sketch = newSketch(context, id + "F2", { "sketchPlane" : qUnion([Q0])});
            skText(sketch, "E50", { "text": "20", "fontName": "OpenSans-Bold.ttf"});
            skCircle(sketch, "E51.0", {"center": v(0.1, -60) * mm, "radius": 71.64 * mm, "construction": true});
            skLineSegment(sketch, "E52.1", {"start": v(0.1, -60) * mm, "end": v(-33.08, 2.65) * mm, "construction": true});
            skLineSegment(sketch, "E52.2", {"start": v(0.1, -60) * mm, "end": v(-32.19, 3.1) * mm, "construction": true});
            skLineSegment(sketch, "E53", {"start": v(-33.08, 2.65) * mm, "end": v(-32.19, 3.1) * mm, "construction": true});
            skLineSegment(sketch, "E54", {"start": v(-32.63, 2.88) * mm, "end": v(-33.32, 4.2) * mm, "construction": true});
            skText(sketch, "E55", { "text": "10", "fontName": "OpenSans-Bold.ttf"});
            skLineSegment(sketch, "E56.0", {"start": v(0.1, -60) * mm, "end": v(-24.25, 5.1) * mm, "construction": true});
            skLineSegment(sketch, "E56.1", {"start": v(0.1, -60) * mm, "end": v(-23.78, 5.27) * mm, "construction": true});
            skLineSegment(sketch, "E56.2", {"start": v(0.1, -60) * mm, "end": v(-18.25, 7.03) * mm, "construction": true});
            skLineSegment(sketch, "E56.3", {"start": v(0.1, -60) * mm, "end": v(-17.77, 7.16) * mm, "construction": true});
            skLineSegment(sketch, "E56.4", {"start": v(-12.57, 8.33) * mm, "end": v(0.1, -60) * mm});
            skLineSegment(sketch, "E56.5", {"start": v(0.1, -60) * mm, "end": v(-12.08, 8.42) * mm, "construction": true});
            skLineSegment(sketch, "E56.6", {"start": v(0.1, -60) * mm, "end": v(-5.49, 9.27) * mm, "construction": true});
            skLineSegment(sketch, "E56.7", {"start": v(0.1, -60) * mm, "end": v(-5, 9.31) * mm, "construction": true});
            skLineSegment(sketch, "E56.8", {"start": v(0.1, -60) * mm, "end": v(-1.42, 9.48) * mm, "construction": true});
            skLineSegment(sketch, "E56.9", {"start": v(0.1, -60) * mm, "end": v(-0.92, 9.5) * mm, "construction": true});
            skLineSegment(sketch, "E56.10", {"start": v(0.1, -60) * mm, "end": v(4.35, 9.37) * mm, "construction": true});
            skLineSegment(sketch, "E56.11", {"start": v(0.1, -60) * mm, "end": v(4.85, 9.34) * mm, "construction": true});
            skLineSegment(sketch, "E56.12", {"start": v(0.1, -60) * mm, "end": v(9.42, 8.87) * mm, "construction": true});
            skLineSegment(sketch, "E56.13", {"start": v(0.1, -60) * mm, "end": v(10.62, 8.7) * mm, "construction": true});
            skLineSegment(sketch, "E56.14", {"start": v(0.1, -60) * mm, "end": v(15.62, 7.74) * mm, "construction": true});
            skLineSegment(sketch, "E56.15", {"start": v(0.1, -60) * mm, "end": v(16.6, 7.51) * mm, "construction": true});
            skLineSegment(sketch, "E56.16", {"start": v(0.1, -60) * mm, "end": v(24.1, 5.23) * mm});
            skLineSegment(sketch, "E56.17", {"start": v(0.1, -60) * mm, "end": v(25.03, 4.87) * mm, "construction": true});
            skLineSegment(sketch, "E56.18", {"start": v(0.1, -60) * mm, "end": v(32.18, 3.22) * mm, "construction": true});
            skLineSegment(sketch, "E56.19", {"start": v(0.1, -60) * mm, "end": v(33.07, 2.76) * mm, "construction": true});
            skLineSegment(sketch, "E57", {"start": v(-24.25, 5.1) * mm, "end": v(-23.78, 5.27) * mm, "construction": true});
            skLineSegment(sketch, "E58", {"start": v(-24.01, 5.18) * mm, "end": v(-24.7, 7.06) * mm, "construction": true});
            skText(sketch, "E59", { "text": "7", "fontName": "OpenSans-Bold.ttf"});
            skLineSegment(sketch, "E60", {"start": v(-18, 7.1) * mm, "end": v(-18.53, 9.03) * mm, "construction": true});
            skLineSegment(sketch, "E61", {"start": v(-18.25, 7.03) * mm, "end": v(-17.77, 7.16) * mm});
            skLineSegment(sketch, "E62", {"start": v(-12.57, 8.33) * mm, "end": v(-12.08, 8.42) * mm, "construction": true});
            skText(sketch, "E63", { "text": "5", "fontName": "OpenSans-Bold.ttf"});
            skLineSegment(sketch, "E64", {"start": v(-12.33, 8.38) * mm, "end": v(-12.69, 10.35) * mm, "construction": true});
            skText(sketch, "E65", { "text": "3", "fontName": "OpenSans-Bold.ttf"});
            skText(sketch, "E66", { "text": "2", "fontName": "OpenSans-Bold.ttf"});
            skText(sketch, "E67", { "text": "1", "fontName": "OpenSans-Bold.ttf"});
            skLineSegment(sketch, "E68", {"start": v(-5.49, 9.27) * mm, "end": v(-5, 9.31) * mm});
            skLineSegment(sketch, "E69", {"start": v(-1.42, 9.48) * mm, "end": v(-0.92, 9.5) * mm});
            skLineSegment(sketch, "E70", {"start": v(4.35, 9.37) * mm, "end": v(4.85, 9.34) * mm});
            skLineSegment(sketch, "E71", {"start": v(-5.24, 9.3) * mm, "end": v(-5.35, 10.79) * mm});
            skLineSegment(sketch, "E72", {"start": v(-1.17, 9.49) * mm, "end": v(-1.2, 10.99) * mm});
            skLineSegment(sketch, "E73", {"start": v(4.6, 9.35) * mm, "end": v(4.7, 10.85) * mm});
            skText(sketch, "E74", { "text": "0", "fontName": "OpenSans-Bold.ttf"});
            skText(sketch, "E75", { "text": "1", "fontName": "OpenSans-Bold.ttf"});
            skText(sketch, "E76", { "text": "2", "fontName": "OpenSans-Bold.ttf"});
            skText(sketch, "E77", { "text": "3", "fontName": "OpenSans-Bold.ttf"});
            skLineSegment(sketch, "E78", {"start": v(9.42, 8.87) * mm, "end": v(10.62, 8.7) * mm});
            skLineSegment(sketch, "E79", {"start": v(15.62, 7.74) * mm, "end": v(16.6, 7.51) * mm});
            skLineSegment(sketch, "E80", {"start": v(24.1, 5.23) * mm, "end": v(25.03, 4.87) * mm});
            skLineSegment(sketch, "E81", {"start": v(32.18, 3.22) * mm, "end": v(33.07, 2.76) * mm});
            skLineSegment(sketch, "E82", {"start": v(10.02, 8.79) * mm, "end": v(10.3, 10.77) * mm});
            skLineSegment(sketch, "E83", {"start": v(16.1, 7.63) * mm, "end": v(16.57, 9.58) * mm});
            skLineSegment(sketch, "E84", {"start": v(24.57, 5.05) * mm, "end": v(25.27, 6.92) * mm});
            skLineSegment(sketch, "E85", {"start": v(32.62, 2.99) * mm, "end": v(33.31, 4.32) * mm});
            skPoint(sketch, "E85.startSnap0", {"position": v(32.62, 2.99) * mm});
            const initialGuessF2  = {"E50": [-0.03625, 0.0042, 1, 0, 0.0036], "E55": [-0.02715, 0.00706, 1, 0, 0.003], "E59": [-0.01979, 0.00903, 1, 0, 0.003], "E63": [-0.01392, 0.01035, 1, 0, 0.003], "E65": [-0.0064, 0.01079, 1, 0, 0.0025], "E66": [-0.00225, 0.01099, 1, 0, 0.0025], "E67": [0.00387, 0.01085, 1, 0, 0.0025], "E74": [0.00905, 0.01077, 1, 0, 0.003], "E75": [0.01557, 0.00958, 1, 0, 0.003], "E76": [0.02401, 0.00692, 1, 0, 0.003], "E77": [0.03182, 0.00432, 1, 0, 0.0036]};
            skSetInitialGuess(sketch, initialGuessF2);
            skSolve(sketch);
        }
        {
            var Q0;
            Q0=qSketchRegion(id+"F2",true);
            extrude(context, id + "F3", {"entities" : qUnion([Q0]), "operationType" : NewBodyOperationType.REMOVE, "endBound" : BoundingType.THROUGH_ALL, "oppositeDirection" : true, "depth" : 5 * mm, "offsetDistance" : 25 * mm});
        }
        {
            var Q0;
            {var subQ7=sQuery(id+"F2.wireOp",EDGE,"E80");Q0=makeQuery(id+"F2.imprint","IMPRINT",FACE,{"disambiguationData":[TD([[makeQuery(id+"F2.imprint","IMPRINT",EDGE,{"derivedFrom":subQ7}),-1.0]])]});}
            var sketch = newSketch(context, id + "F4", { "sketchPlane" : qUnion([Q0])});
            skLineSegment(sketch, "E86.0.0", {"start": v(22.72, 1.47) * mm, "end": v(14.5, -20.84) * mm});
            skLineSegment(sketch, "E86.0.1", {"start": v(14.5, -20.84) * mm, "end": v(43.08, -20.84) * mm});
            skLineSegment(sketch, "E86.0.2", {"start": v(43.08, -20.84) * mm, "end": v(43.08, 19.18) * mm});
            skLineSegment(sketch, "E86.0.3", {"start": v(43.08, 19.18) * mm, "end": v(-43.08, 19.18) * mm});
            skLineSegment(sketch, "E86.0.4", {"start": v(-43.08, 19.18) * mm, "end": v(-43.08, -20.84) * mm});
            skLineSegment(sketch, "E86.0.5", {"start": v(-43.08, -20.84) * mm, "end": v(-7.16, -20.84) * mm});
            skLineSegment(sketch, "E86.0.6", {"start": v(-7.16, -20.84) * mm, "end": v(-11.85, 4.4) * mm});
            skArc(sketch, "E86.0.7", {"start": v(-11.85, 4.4) * mm, "mid": v(-21.45, 1.85) * mm, "end": v(-30.55, -2.12) * mm});
            skLineSegment(sketch, "E86.0.8", {"start": v(-30.55, -2.12) * mm, "end": v(-33.08, 2.65) * mm});
            skArc(sketch, "E86.0.9", {"start": v(-33.08, 2.65) * mm, "mid": v(-32.63, 2.88) * mm, "end": v(-32.19, 3.1) * mm});
            skLineSegment(sketch, "E86.0.10", {"start": v(-32.19, 3.1) * mm, "end": v(-30.19, -0.8) * mm});
            skArc(sketch, "E86.0.11", {"start": v(-30.19, -0.8) * mm, "mid": v(-26.74, 0.84) * mm, "end": v(-23.2, 2.29) * mm});
            skLineSegment(sketch, "E86.0.12", {"start": v(-23.2, 2.29) * mm, "end": v(-24.25, 5.1) * mm});
            skArc(sketch, "E86.0.13", {"start": v(-24.25, 5.1) * mm, "mid": v(-24.01, 5.18) * mm, "end": v(-23.78, 5.27) * mm});
            skLineSegment(sketch, "E86.0.14", {"start": v(-23.78, 5.27) * mm, "end": v(-22.75, 2.45) * mm});
            skArc(sketch, "E86.0.15", {"start": v(-22.75, 2.45) * mm, "mid": v(-20.12, 3.35) * mm, "end": v(-17.46, 4.14) * mm});
            skLineSegment(sketch, "E86.0.16", {"start": v(-17.46, 4.14) * mm, "end": v(-18.25, 7.03) * mm});
            skArc(sketch, "E86.0.17", {"start": v(-18.25, 7.03) * mm, "mid": v(-18, 7.1) * mm, "end": v(-17.77, 7.16) * mm});
            skLineSegment(sketch, "E86.0.18", {"start": v(-17.77, 7.16) * mm, "end": v(-17, 4.27) * mm});
            skArc(sketch, "E86.0.19", {"start": v(-17, 4.27) * mm, "mid": v(-14.52, 4.87) * mm, "end": v(-12.03, 5.38) * mm});
            skLineSegment(sketch, "E86.0.20", {"start": v(-12.03, 5.38) * mm, "end": v(-12.57, 8.33) * mm});
            skArc(sketch, "E86.0.21", {"start": v(-12.57, 8.33) * mm, "mid": v(-12.33, 8.38) * mm, "end": v(-12.08, 8.42) * mm});
            skLineSegment(sketch, "E86.0.22", {"start": v(-12.08, 8.42) * mm, "end": v(-11.56, 5.47) * mm});
            skArc(sketch, "E86.0.23", {"start": v(-11.56, 5.47) * mm, "mid": v(-8.41, 5.95) * mm, "end": v(-5.25, 6.28) * mm});
            skLineSegment(sketch, "E86.0.24", {"start": v(-5.25, 6.28) * mm, "end": v(-5.49, 9.27) * mm});
            skArc(sketch, "E86.0.25", {"start": v(-5.49, 9.27) * mm, "mid": v(-5.36, 9.28) * mm, "end": v(-5.24, 9.3) * mm});
            skArc(sketch, "E86.0.26", {"start": v(-5.24, 9.3) * mm, "mid": v(-5.11, 9.3) * mm, "end": v(-5, 9.31) * mm});
            skLineSegment(sketch, "E86.0.27", {"start": v(-5, 9.31) * mm, "end": v(-4.77, 6.32) * mm});
            skArc(sketch, "E86.0.28", {"start": v(-4.77, 6.32) * mm, "mid": v(-3.07, 6.42) * mm, "end": v(-1.36, 6.48) * mm});
            skLineSegment(sketch, "E86.0.29", {"start": v(-1.36, 6.48) * mm, "end": v(-1.42, 9.48) * mm});
            skArc(sketch, "E86.0.30", {"start": v(-1.42, 9.48) * mm, "mid": v(-1.3, 9.49) * mm, "end": v(-1.17, 9.49) * mm});
            skArc(sketch, "E86.0.31", {"start": v(-1.17, 9.49) * mm, "mid": v(-1.05, 9.5) * mm, "end": v(-0.92, 9.5) * mm});
            skLineSegment(sketch, "E86.0.32", {"start": v(-0.92, 9.5) * mm, "end": v(-0.88, 6.5) * mm});
            skArc(sketch, "E86.0.33", {"start": v(-0.88, 6.5) * mm, "mid": v(1.64, 6.48) * mm, "end": v(4.16, 6.38) * mm});
            skLineSegment(sketch, "E86.0.34", {"start": v(4.16, 6.38) * mm, "end": v(4.35, 9.37) * mm});
            skArc(sketch, "E86.0.35", {"start": v(4.35, 9.37) * mm, "mid": v(4.47, 9.36) * mm, "end": v(4.6, 9.35) * mm});
            skArc(sketch, "E86.0.36", {"start": v(4.6, 9.35) * mm, "mid": v(4.72, 9.35) * mm, "end": v(4.85, 9.34) * mm});
            skLineSegment(sketch, "E86.0.37", {"start": v(4.85, 9.34) * mm, "end": v(4.64, 6.34) * mm});
            skArc(sketch, "E86.0.38", {"start": v(4.64, 6.34) * mm, "mid": v(6.83, 6.16) * mm, "end": v(9.02, 5.9) * mm});
            skLineSegment(sketch, "E86.0.39", {"start": v(9.02, 5.9) * mm, "end": v(9.42, 8.87) * mm});
            skArc(sketch, "E86.0.40", {"start": v(9.42, 8.87) * mm, "mid": v(9.72, 8.83) * mm, "end": v(10.02, 8.79) * mm});
            skArc(sketch, "E86.0.41", {"start": v(10.02, 8.79) * mm, "mid": v(10.32, 8.74) * mm, "end": v(10.62, 8.7) * mm});
            skLineSegment(sketch, "E86.0.42", {"start": v(10.62, 8.7) * mm, "end": v(10.35, 6.97) * mm});
            skArc(sketch, "E86.0.43", {"start": v(10.35, 6.97) * mm, "mid": v(12.8, 6.55) * mm, "end": v(15.23, 6.04) * mm});
            skLineSegment(sketch, "E86.0.44", {"start": v(15.23, 6.04) * mm, "end": v(15.62, 7.74) * mm});
            skArc(sketch, "E86.0.45", {"start": v(15.62, 7.74) * mm, "mid": v(15.86, 7.69) * mm, "end": v(16.1, 7.63) * mm});
            skArc(sketch, "E86.0.46", {"start": v(16.1, 7.63) * mm, "mid": v(16.35, 7.57) * mm, "end": v(16.6, 7.51) * mm});
            skLineSegment(sketch, "E86.0.47", {"start": v(16.6, 7.51) * mm, "end": v(16.18, 5.81) * mm});
            skArc(sketch, "E86.0.48", {"start": v(16.18, 5.81) * mm, "mid": v(19.87, 4.8) * mm, "end": v(23.5, 3.58) * mm});
            skLineSegment(sketch, "E86.0.49", {"start": v(23.5, 3.58) * mm, "end": v(24.1, 5.23) * mm});
            skArc(sketch, "E86.0.50", {"start": v(24.1, 5.23) * mm, "mid": v(24.33, 5.14) * mm, "end": v(24.57, 5.05) * mm});
            skArc(sketch, "E86.0.51", {"start": v(24.57, 5.05) * mm, "mid": v(24.8, 4.96) * mm, "end": v(25.03, 4.87) * mm});
            skLineSegment(sketch, "E86.0.52", {"start": v(25.03, 4.87) * mm, "end": v(24.4, 3.24) * mm});
            skArc(sketch, "E86.0.53", {"start": v(24.4, 3.24) * mm, "mid": v(27.62, 1.9) * mm, "end": v(30.76, 0.42) * mm});
            skLineSegment(sketch, "E86.0.54", {"start": v(30.76, 0.42) * mm, "end": v(32.18, 3.22) * mm});
            skArc(sketch, "E86.0.55", {"start": v(32.18, 3.22) * mm, "mid": v(32.4, 3.1) * mm, "end": v(32.62, 2.99) * mm});
            skArc(sketch, "E86.0.56", {"start": v(32.62, 2.99) * mm, "mid": v(32.85, 2.87) * mm, "end": v(33.07, 2.76) * mm});
            skLineSegment(sketch, "E86.0.57", {"start": v(33.07, 2.76) * mm, "end": v(30.56, -2.01) * mm});
            skArc(sketch, "E86.0.58", {"start": v(30.56, -2.01) * mm, "mid": v(26.7, -0.14) * mm, "end": v(22.72, 1.47) * mm});
            skLineSegment(sketch, "E87.0", {"start": v(0.1, -60) * mm, "end": v(9.42, 8.87) * mm});
            skCircle(sketch, "E88.0", {"center": v(0.1, -60) * mm, "radius": 65.5 * mm});
            skSolve(sketch);
        }
        {
            var Q0;
            {var subQ7=sQuery(id+"F4.wireOp",EDGE,"E86.0.40");Q0=makeQuery(id+"F4.imprint","IMPRINT",FACE,{"disambiguationData":[TD([[makeQuery(id+"F4.imprint","IMPRINT",EDGE,{"derivedFrom":subQ7}),-1.0]])]});}
            var Q1;
            Q1=makeQuery(id+"F4.imprint","IMPRINT",FACE,{"disambiguationData":[TD([[makeQuery(id+"F4.imprint","IMPRINT",EDGE,{"derivedFrom":sQuery(id+"F4.wireOp",EDGE,"E86.0.49")}),-1.0]])]});
            extrude(context, id + "F5", {"entities" : qUnion([Q0, Q1]), "depth" : 2 * mm, "offsetDistance" : 25 * mm});
        }
        {
            var Q0;
            {var subQ4=sQuery(id+"F4.wireOp",EDGE,"E86.0.8");Q0=makeQuery(id+"F4.imprint","IMPRINT",FACE,{"disambiguationData":[TD([[makeQuery(id+"F4.imprint","IMPRINT",EDGE,{"derivedFrom":subQ4}),-1.0]])]});}
            extrude(context, id + "F6", {"entities" : qUnion([Q0]), "depth" : 2 * mm, "offsetDistance" : 25 * mm});
        }
        {
            var Q0;
            Q0=qCreatedBy(makeId("Top.planeOp"),FACE);
            cPlane(context, id + "F7", {"entities" : qUnion([Q0]), "cplaneType" : CPlaneType.OFFSET, "offset" : 7 * mm, "width" : 150 * mm, "height" : 150 * mm});
        }
        {
            var Q0;
            Q0=qCreatedBy(id+"F7.planeOp",FACE);
            var sketch = newSketch(context, id + "F8", { "sketchPlane" : qUnion([Q0])});
            skLineSegment(sketch, "E89", {"start": v(34.12, -2.75) * mm, "end": v(-7.25, -34.2) * mm});
            skLineSegment(sketch, "E90", {"start": v(0, -60.06) * mm, "end": v(0, -28.68) * mm, "construction": true});
            skCircle(sketch, "E91", {"center": v(0, -28.68) * mm, "radius": 2.5 * mm});
            skLineSegment(sketch, "E92", {"start": v(-7.25, -34.2) * mm, "end": v(-6.95, -34.6) * mm});
            skLineSegment(sketch, "E93", {"start": v(34.12, -2.75) * mm, "end": v(34.42, -3.14) * mm});
            skLineSegment(sketch, "E94", {"start": v(34.42, -3.14) * mm, "end": v(-6.95, -34.6) * mm});
            skLineSegment(sketch, "E95.MirrorCS", {"start": v(33.81, -2.35) * mm, "end": v(-7.56, -33.8) * mm});
            skLineSegment(sketch, "E96.MirrorCS", {"start": v(34.12, -2.75) * mm, "end": v(33.81, -2.35) * mm});
            skLineSegment(sketch, "E97.MirrorCS", {"start": v(-7.25, -34.2) * mm, "end": v(-7.56, -33.8) * mm});
            skSolve(sketch);
        }
        {
            var Q0;
            {var subQ0=sQuery(id+"F8.wireOp",EDGE,"E94");var subQ1=sQuery(id+"F8.wireOp",EDGE,"E91");var subQ2=makeQuery(id+"F8.imprint","INTERSECT",VERTEX,{"disambiguationData":[OD(0.0)],"derivedFrom":[subQ1,subQ0]});Q0=makeQuery(id+"F8.imprint","IMPRINT",FACE,{"disambiguationData":[TD([[makeQuery(id+"F8.imprint","IMPRINT",EDGE,{"disambiguationData":[TD([[subQ2,1.0]])],"derivedFrom":subQ1}),1.0]])]});}
            var Q1;
            {var subQ0=sQuery(id+"F8.wireOp",EDGE,"E95.MirrorCS");var subQ1=sQuery(id+"F8.wireOp",EDGE,"E91");var subQ2=makeQuery(id+"F8.imprint","INTERSECT",VERTEX,{"disambiguationData":[OD(0.0)],"derivedFrom":[subQ1,subQ0]});Q1=makeQuery(id+"F8.imprint","IMPRINT",FACE,{"disambiguationData":[TD([[makeQuery(id+"F8.imprint","IMPRINT",EDGE,{"disambiguationData":[TD([[subQ2,-1.0]])],"derivedFrom":subQ1}),1.0]])]});}
            var Q2;
            {var subQ0=sQuery(id+"F8.wireOp",EDGE,"E91");var subQ1=sQuery(id+"F8.wireOp",EDGE,"E89");var subQ2=makeQuery(id+"F8.imprint","INTERSECT",VERTEX,{"disambiguationData":[OD(0.0)],"derivedFrom":[subQ1,subQ0]});Q2=makeQuery(id+"F8.imprint","IMPRINT",FACE,{"disambiguationData":[TD([[makeQuery(id+"F8.imprint","IMPRINT",EDGE,{"disambiguationData":[TD([[subQ2,-1.0]])],"derivedFrom":subQ1}),1.0]])]});}
            var Q3;
            {var subQ0=sQuery(id+"F8.wireOp",EDGE,"E91");var subQ1=sQuery(id+"F8.wireOp",EDGE,"E89");var subQ2=makeQuery(id+"F8.imprint","INTERSECT",VERTEX,{"disambiguationData":[OD(0.0)],"derivedFrom":[subQ1,subQ0]});Q3=makeQuery(id+"F8.imprint","IMPRINT",FACE,{"disambiguationData":[TD([[makeQuery(id+"F8.imprint","IMPRINT",EDGE,{"disambiguationData":[TD([[subQ2,-1.0]])],"derivedFrom":subQ1}),-1.0]])]});}
            extrude(context, id + "F9", {"entities" : qUnion([Q0, Q1, Q2, Q3]), "oppositeDirection" : true, "depth" : 25 * mm, "offsetDistance" : 25 * mm});
        }
        {
            var Q0;
            {var subQ0=sQuery(id+"F8.wireOp",EDGE,"E92");Q0=makeQuery(id+"F8.imprint","IMPRINT",FACE,{"disambiguationData":[TD([[makeQuery(id+"F8.imprint","IMPRINT",EDGE,{"derivedFrom":subQ0}),1.0]])]});}
            var Q1;
            {var subQ0=sQuery(id+"F8.wireOp",EDGE,"E93");Q1=makeQuery(id+"F8.imprint","IMPRINT",FACE,{"disambiguationData":[TD([[makeQuery(id+"F8.imprint","IMPRINT",EDGE,{"derivedFrom":subQ0}),-1.0]])]});}
            var Q2;
            {var subQ0=sQuery(id+"F8.wireOp",EDGE,"E91");var subQ1=sQuery(id+"F8.wireOp",EDGE,"E89");var subQ2=makeQuery(id+"F8.imprint","INTERSECT",VERTEX,{"disambiguationData":[OD(0.0)],"derivedFrom":[subQ1,subQ0]});Q2=makeQuery(id+"F8.imprint","IMPRINT",FACE,{"disambiguationData":[TD([[makeQuery(id+"F8.imprint","IMPRINT",EDGE,{"disambiguationData":[TD([[subQ2,-1.0]])],"derivedFrom":subQ1}),1.0]])]});}
            var Q3;
            Q3=sQuery(id+"F8.wireOp",EDGE,"E89");
            revolve(context, id + "F10", {"surfaceOperationType" : NewSurfaceOperationType.NEW, "entities" : qUnion([Q0, Q1, Q2]), "axis" : qUnion([Q3]), "revolveType" : RevolveType.FULL});
        }
    });
